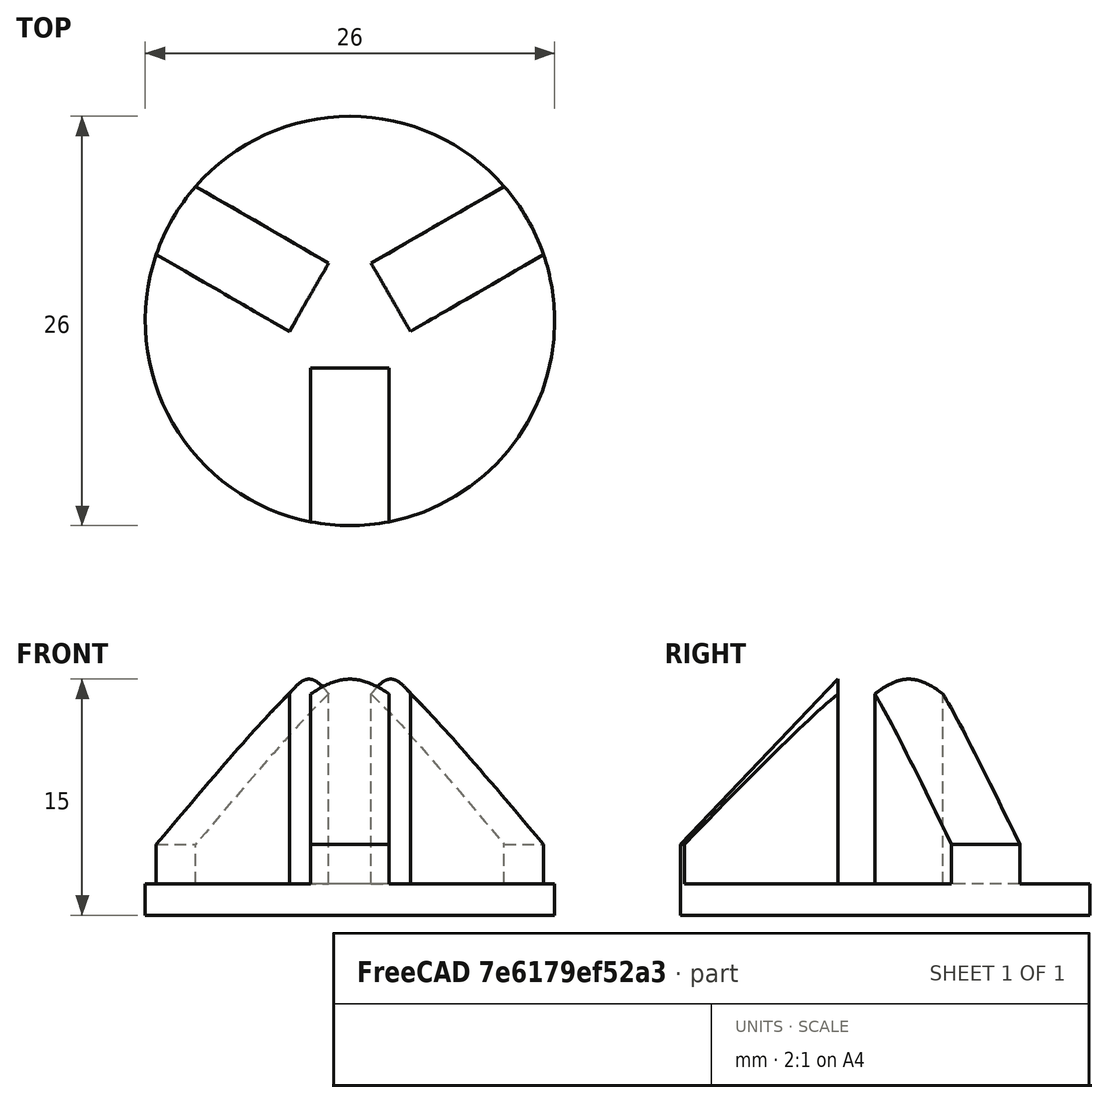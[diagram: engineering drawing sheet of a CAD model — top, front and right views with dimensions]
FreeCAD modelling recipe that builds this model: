
FCSTD DOCUMENT  (FreeCAD 0.18.4R)
Label: 20
License: All rights reserved
LicenseURL: http://en.wikipedia.org/wiki/All_rights_reserved
objects: Sketcher::SketchObject×3, PartDesign::Pad×2, PartDesign::Groove×1, PartDesign::Body×1
note: 10 computed .brp shape members not serialized (recipe doc carries the construction recipe); baked Part::Feature solids carry a one-line shape summary decoded from their .brp

FEATURE [Sketcher::SketchObject] Sketch
  MapMode = 5
  Support = -> [XY_Plane]
  constraints (67):
    c: Coincident(g0,g-1)
    c: Coincident(g1,g0)
    c: Coincident(g2,g1)
    c: Coincident(g3,g2)
    c: Coincident(g4,g0)
    c: Coincident(g4,g3)
    c: Coincident(g5,g4)
    c: Vertical(g5)
    c: Coincident(g6,g5)
    c: Horizontal(g6)
    c: Coincident(g7,g6)
    c: Vertical(g7)
    c: Coincident(g8,g0)
    c: Coincident(g9,g8)
    c: Coincident(g10,g9)
    c: Coincident(g11,g0)
    c: Coincident(g11,g7)
    c: Coincident(g11,g10)
    c: Perpendicular(g10,g9)
    c: Perpendicular(g8,g9)
    c: Perpendicular(g2,g1)
    c: Perpendicular(g2,g3)
    c: Diameter(g4) = 26
    c: Equal(g2,g9)
    c: Equal(g9,g6)
    c: PointOnObject(g12,g9)
    c: PointOnObject(g13,g2)
    c: PointOnObject(g14,g6)
    c: Vertical(g14)
    c: Coincident(g15,g6)
    c: Coincident(g15,g14)
    c: Coincident(g16,g14)
    c: Coincident(g16,g5)
    c: Coincident(g17,g1)
    c: Coincident(g17,g13)
    c: Coincident(g18,g13)
    c: Coincident(g18,g2)
    c: Coincident(g19,g9)
    c: Coincident(g19,g12)
    c: Coincident(g20,g12)
    c: Coincident(g20,g8)
    c: Equal(g12,g13)
    c: Equal(g13,g14)
    c: Equal(g15,g16)
    c: Equal(g16,g17)
    c: Equal(g18,g19)
    c: Perpendicular(g2,g13)
    c: Perpendicular(g9,g12)
    c: PointOnObject(g14,g0)
    c: PointOnObject(g13,g0)
    c: PointOnObject(g12,g0)
    c: Perpendicular(g0,g12)
    c: Perpendicular(g0,g13)
    c: Perpendicular(g0,g14)
    c: Distance(g14) = 10
    c: Distance(g6) = 5
    c: Angle(g13,g12) = 2.0944
    c: Angle(g14,g13) = 2.0944
    c: Coincident(g21,g10)
    c: Coincident(g21,g8)
    c: Coincident(g22,g1)
    c: Coincident(g22,g3)
    c: Coincident(g21,g-1)
    c: Coincident(g22,g21)
    c: Coincident(g23,g7)
    c: Coincident(g23,g5)
    c: PointOnObject(g14,g23)
FEATURE [Sketcher::SketchObject] Sketch001  label="Sketch002"
  MapMode = 5
  Placement = pos=(0,0,0) rot=(1,0,0;1.5708rad)
  Support = -> [XZ_Plane]
  constraints (2):
    c: Coincident(g0,g-1)
    c: Diameter(g0) = 26
FEATURE [PartDesign::Pad] Pad  label="Unnamed"
  Length = 100
  Length2 = 100
  Type = 0
FEATURE [PartDesign::Pad] Pad001  label="Unnamed"
  Length = 100
  Length2 = 100
  Type = 0
FEATURE [Sketcher::SketchObject] Sketch002  label="Unnamed"
FEATURE [PartDesign::Groove] Groove
  Angle = 360
  Axis = (0,2e-16,1)
  Base = (0,0,0)
  BaseFeature = -> Pad001
  Profile = -> Sketch002
  ReferenceAxis = -> Sketch002 [V_Axis]
  Reversed = true
FEATURE [PartDesign::Body] Body
  Group = -> [Sketch,Sketch001,Pad,Pad001,Sketch002,Groove]
  Origin = -> Origin
  Tip = -> Groove
